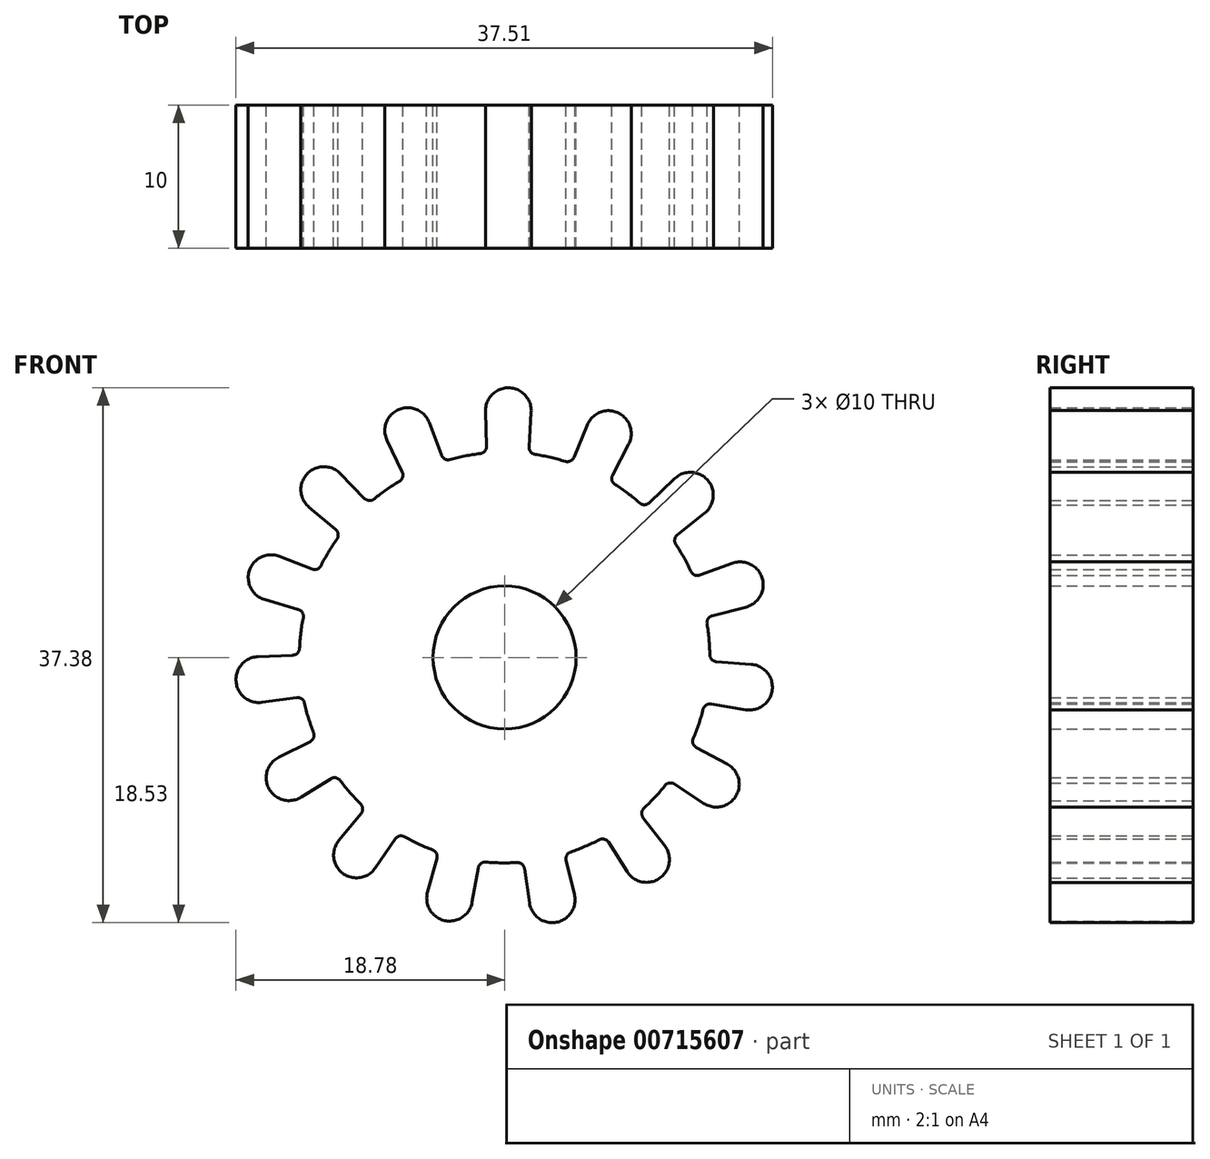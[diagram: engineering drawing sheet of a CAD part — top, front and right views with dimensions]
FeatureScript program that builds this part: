
annotation { "Feature Type Name" : "Feature", "Feature Type Description" : "" }
export const myFeature = defineFeature(function(context is Context, id is Id, definition is map)
    precondition{}
    {
        {
            var Q0;
            Q0=qCreatedBy(makeId("Front.planeOp"),FACE);
            var sketch = newSketch(context, id + "F0", { "sketchPlane" : qUnion([Q0])});
            skCircle(sketch, "E0", {"center": v(0, 0) * mm, "radius": 5 * mm});
            skCircle(sketch, "E1", {"center": v(0, 0) * mm, "radius": 14.35 * mm});
            skCircle(sketch, "E2", {"center": v(0, 0) * mm, "radius": 17.25 * mm, "construction": true});
            skCircle(sketch, "E3", {"center": v(0.26, 17.25) * mm, "radius": 1.6 * mm});
            skLineSegment(sketch, "E4", {"start": v(-1.34, 17.2) * mm, "end": v(-1.26, 14.76) * mm});
            skArc(sketch, "E5", {"start": v(1.71, 14.72) * mm, "mid": v(1.82, 14.37) * mm, "end": v(2.14, 14.2) * mm});
            skArc(sketch, "E6", {"start": v(-1.7, 14.25) * mm, "mid": v(-1.38, 14.42) * mm, "end": v(-1.26, 14.76) * mm});
            skLineSegment(sketch, "E7", {"start": v(1.86, 17.15) * mm, "end": v(1.71, 14.72) * mm});
            skCircle(sketch, "E8.1.0", {"center": v(-6.77, 15.86) * mm, "radius": 1.6 * mm});
            skLineSegment(sketch, "E8.1.1", {"start": v(-5.28, 16.42) * mm, "end": v(-4.42, 14.14) * mm});
            skLineSegment(sketch, "E8.1.2", {"start": v(-8.22, 15.17) * mm, "end": v(-7.15, 12.97) * mm});
            skArc(sketch, "E8.1.3", {"start": v(-7.35, 12.33) * mm, "mid": v(-7.13, 12.61) * mm, "end": v(-7.15, 12.97) * mm});
            skArc(sketch, "E8.1.4", {"start": v(-4.42, 14.14) * mm, "mid": v(-4.18, 13.87) * mm, "end": v(-3.82, 13.83) * mm});
            skCircle(sketch, "E8.2.0", {"center": v(-12.64, 11.74) * mm, "radius": 1.6 * mm});
            skLineSegment(sketch, "E8.2.1", {"start": v(-11.5, 12.86) * mm, "end": v(-9.8, 11.12) * mm});
            skLineSegment(sketch, "E8.2.2", {"start": v(-13.67, 10.52) * mm, "end": v(-11.81, 8.94) * mm});
            skArc(sketch, "E8.2.3", {"start": v(-11.73, 8.27) * mm, "mid": v(-11.64, 8.62) * mm, "end": v(-11.81, 8.94) * mm});
            skArc(sketch, "E8.2.4", {"start": v(-9.8, 11.12) * mm, "mid": v(-9.46, 10.97) * mm, "end": v(-9.12, 11.08) * mm});
            skCircle(sketch, "E9.1.3.0", {"center": v(-16.32, 5.58) * mm, "radius": 1.6 * mm});
            skLineSegment(sketch, "E9.2.3.0", {"start": v(-15.73, 7.07) * mm, "end": v(-13.47, 6.17) * mm});
            skLineSegment(sketch, "E9.5.3.0", {"start": v(-16.77, 4.04) * mm, "end": v(-14.43, 3.36) * mm});
            skArc(sketch, "E9.8.3.0", {"start": v(-14.08, 2.79) * mm, "mid": v(-14.14, 3.14) * mm, "end": v(-14.43, 3.36) * mm});
            skArc(sketch, "E9.12.3.0", {"start": v(-13.47, 6.17) * mm, "mid": v(-13.1, 6.17) * mm, "end": v(-12.84, 6.42) * mm});
            skCircle(sketch, "E9.1.4.0", {"center": v(-17.18, -1.54) * mm, "radius": 1.6 * mm});
            skLineSegment(sketch, "E9.2.4.0", {"start": v(-17.25, 0.06) * mm, "end": v(-14.81, 0.16) * mm});
            skLineSegment(sketch, "E9.5.4.0", {"start": v(-16.96, -3.13) * mm, "end": v(-14.55, -2.8) * mm});
            skArc(sketch, "E9.8.4.0", {"start": v(-14, -3.18) * mm, "mid": v(-14.2, -2.88) * mm, "end": v(-14.55, -2.8) * mm});
            skArc(sketch, "E9.12.4.0", {"start": v(-14.81, 0.16) * mm, "mid": v(-14.48, 0.3) * mm, "end": v(-14.34, 0.64) * mm});
            skCircle(sketch, "E9.1.5.0", {"center": v(-15.07, -8.4) * mm, "radius": 1.6 * mm});
            skLineSegment(sketch, "E9.2.5.0", {"start": v(-15.78, -6.96) * mm, "end": v(-13.6, -5.88) * mm});
            skLineSegment(sketch, "E9.5.5.0", {"start": v(-14.23, -9.76) * mm, "end": v(-12.15, -8.47) * mm});
            skArc(sketch, "E9.8.5.0", {"start": v(-11.49, -8.6) * mm, "mid": v(-11.8, -8.4) * mm, "end": v(-12.15, -8.47) * mm});
            skArc(sketch, "E9.12.5.0", {"start": v(-13.6, -5.88) * mm, "mid": v(-13.36, -5.6) * mm, "end": v(-13.36, -5.25) * mm});
            skCircle(sketch, "E9.1.6.0", {"center": v(-10.35, -13.8) * mm, "radius": 1.6 * mm});
            skLineSegment(sketch, "E9.2.6.0", {"start": v(-11.59, -12.78) * mm, "end": v(-10.03, -10.9) * mm});
            skLineSegment(sketch, "E9.5.6.0", {"start": v(-9.03, -14.7) * mm, "end": v(-7.66, -12.68) * mm});
            skArc(sketch, "E9.8.6.0", {"start": v(-7, -12.53) * mm, "mid": v(-7.36, -12.48) * mm, "end": v(-7.66, -12.68) * mm});
            skArc(sketch, "E9.12.6.0", {"start": v(-10.03, -10.9) * mm, "mid": v(-9.92, -10.56) * mm, "end": v(-10.07, -10.23) * mm});
            skCircle(sketch, "E9.1.7.0", {"center": v(-3.84, -16.82) * mm, "radius": 1.6 * mm});
            skLineSegment(sketch, "E9.2.7.0", {"start": v(-5.39, -16.39) * mm, "end": v(-4.73, -14.04) * mm});
            skLineSegment(sketch, "E9.5.7.0", {"start": v(-2.27, -17.1) * mm, "end": v(-1.84, -14.7) * mm});
            skArc(sketch, "E9.8.7.0", {"start": v(-1.3, -14.3) * mm, "mid": v(-1.65, -14.4) * mm, "end": v(-1.84, -14.7) * mm});
            skArc(sketch, "E9.12.7.0", {"start": v(-4.73, -14.04) * mm, "mid": v(-4.77, -13.68) * mm, "end": v(-5.04, -13.44) * mm});
            skCircle(sketch, "E9.1.8.0", {"center": v(3.33, -16.93) * mm, "radius": 1.6 * mm});
            skLineSegment(sketch, "E9.2.8.0", {"start": v(1.75, -17.16) * mm, "end": v(1.39, -14.75) * mm});
            skLineSegment(sketch, "E9.5.8.0", {"start": v(4.88, -16.54) * mm, "end": v(4.3, -14.18) * mm});
            skArc(sketch, "E9.8.8.0", {"start": v(4.63, -13.58) * mm, "mid": v(4.35, -13.82) * mm, "end": v(4.3, -14.18) * mm});
            skArc(sketch, "E9.12.8.0", {"start": v(1.39, -14.75) * mm, "mid": v(1.2, -14.43) * mm, "end": v(0.86, -14.32) * mm});
            skCircle(sketch, "E9.1.9.0", {"center": v(9.92, -14.1) * mm, "radius": 1.6 * mm});
            skLineSegment(sketch, "E9.2.9.0", {"start": v(8.57, -14.97) * mm, "end": v(7.27, -12.91) * mm});
            skLineSegment(sketch, "E9.5.9.0", {"start": v(11.19, -13.13) * mm, "end": v(9.7, -11.2) * mm});
            skArc(sketch, "E9.8.9.0", {"start": v(9.75, -10.53) * mm, "mid": v(9.6, -10.85) * mm, "end": v(9.7, -11.2) * mm});
            skArc(sketch, "E9.12.9.0", {"start": v(7.27, -12.91) * mm, "mid": v(6.97, -12.7) * mm, "end": v(6.61, -12.74) * mm});
            skCircle(sketch, "E9.1.10.0", {"center": v(14.8, -8.85) * mm, "radius": 1.6 * mm});
            skLineSegment(sketch, "E9.2.10.0", {"start": v(13.92, -10.19) * mm, "end": v(11.89, -8.84) * mm});
            skLineSegment(sketch, "E9.5.10.0", {"start": v(15.56, -7.44) * mm, "end": v(13.41, -6.29) * mm});
            skArc(sketch, "E9.8.10.0", {"start": v(13.19, -5.65) * mm, "mid": v(13.18, -6.01) * mm, "end": v(13.41, -6.29) * mm});
            skArc(sketch, "E9.12.10.0", {"start": v(11.89, -8.84) * mm, "mid": v(11.53, -8.76) * mm, "end": v(11.22, -8.94) * mm});
            skCircle(sketch, "E9.1.11.0", {"center": v(17.13, -2.07) * mm, "radius": 1.6 * mm});
            skLineSegment(sketch, "E9.2.11.0", {"start": v(16.86, -3.64) * mm, "end": v(14.46, -3.24) * mm});
            skLineSegment(sketch, "E9.5.11.0", {"start": v(17.24, -0.47) * mm, "end": v(14.81, -0.3) * mm});
            skArc(sketch, "E9.8.11.0", {"start": v(14.35, 0.2) * mm, "mid": v(14.48, -0.13) * mm, "end": v(14.81, -0.3) * mm});
            skArc(sketch, "E9.12.11.0", {"start": v(14.46, -3.24) * mm, "mid": v(14.1, -3.31) * mm, "end": v(13.89, -3.6) * mm});
            skCircle(sketch, "E9.1.12.0", {"center": v(16.49, 5.08) * mm, "radius": 1.6 * mm});
            skLineSegment(sketch, "E9.2.12.0", {"start": v(16.89, 3.53) * mm, "end": v(14.52, 2.92) * mm});
            skLineSegment(sketch, "E9.5.12.0", {"start": v(15.94, 6.58) * mm, "end": v(13.65, 5.76) * mm});
            skArc(sketch, "E9.8.12.0", {"start": v(13.03, 6.02) * mm, "mid": v(13.29, 5.77) * mm, "end": v(13.65, 5.76) * mm});
            skArc(sketch, "E9.12.12.0", {"start": v(14.52, 2.92) * mm, "mid": v(14.23, 2.7) * mm, "end": v(14.16, 2.35) * mm});
            skCircle(sketch, "E9.1.13.0", {"center": v(13, 11.35) * mm, "radius": 1.6 * mm});
            skLineSegment(sketch, "E9.2.13.0", {"start": v(13.99, 10.1) * mm, "end": v(12.08, 8.58) * mm});
            skLineSegment(sketch, "E9.5.13.0", {"start": v(11.89, 12.5) * mm, "end": v(10.13, 10.81) * mm});
            skArc(sketch, "E9.8.13.0", {"start": v(9.45, 10.8) * mm, "mid": v(9.8, 10.67) * mm, "end": v(10.13, 10.81) * mm});
            skArc(sketch, "E9.12.13.0", {"start": v(12.08, 8.58) * mm, "mid": v(11.9, 8.26) * mm, "end": v(11.97, 7.9) * mm});
            skCircle(sketch, "E9.1.14.0", {"center": v(7.26, 15.65) * mm, "radius": 1.6 * mm});
            skLineSegment(sketch, "E9.2.14.0", {"start": v(8.68, 14.9) * mm, "end": v(7.55, 12.75) * mm});
            skLineSegment(sketch, "E9.5.14.0", {"start": v(5.78, 16.25) * mm, "end": v(4.85, 14) * mm});
            skArc(sketch, "E9.8.14.0", {"start": v(4.24, 13.7) * mm, "mid": v(4.6, 13.73) * mm, "end": v(4.85, 14) * mm});
            skArc(sketch, "E9.12.14.0", {"start": v(7.55, 12.75) * mm, "mid": v(7.5, 12.39) * mm, "end": v(7.72, 12.1) * mm});
            skSolve(sketch);
        }
        {
            var Q0;
            Q0 = qSketchRegion(id + "F0", true);
            extrude(context, id + "F1", {"entities" : qUnion([Q0]), "depth" : 10 * mm, "offsetDistance" : 25 * mm});
        }
    });
